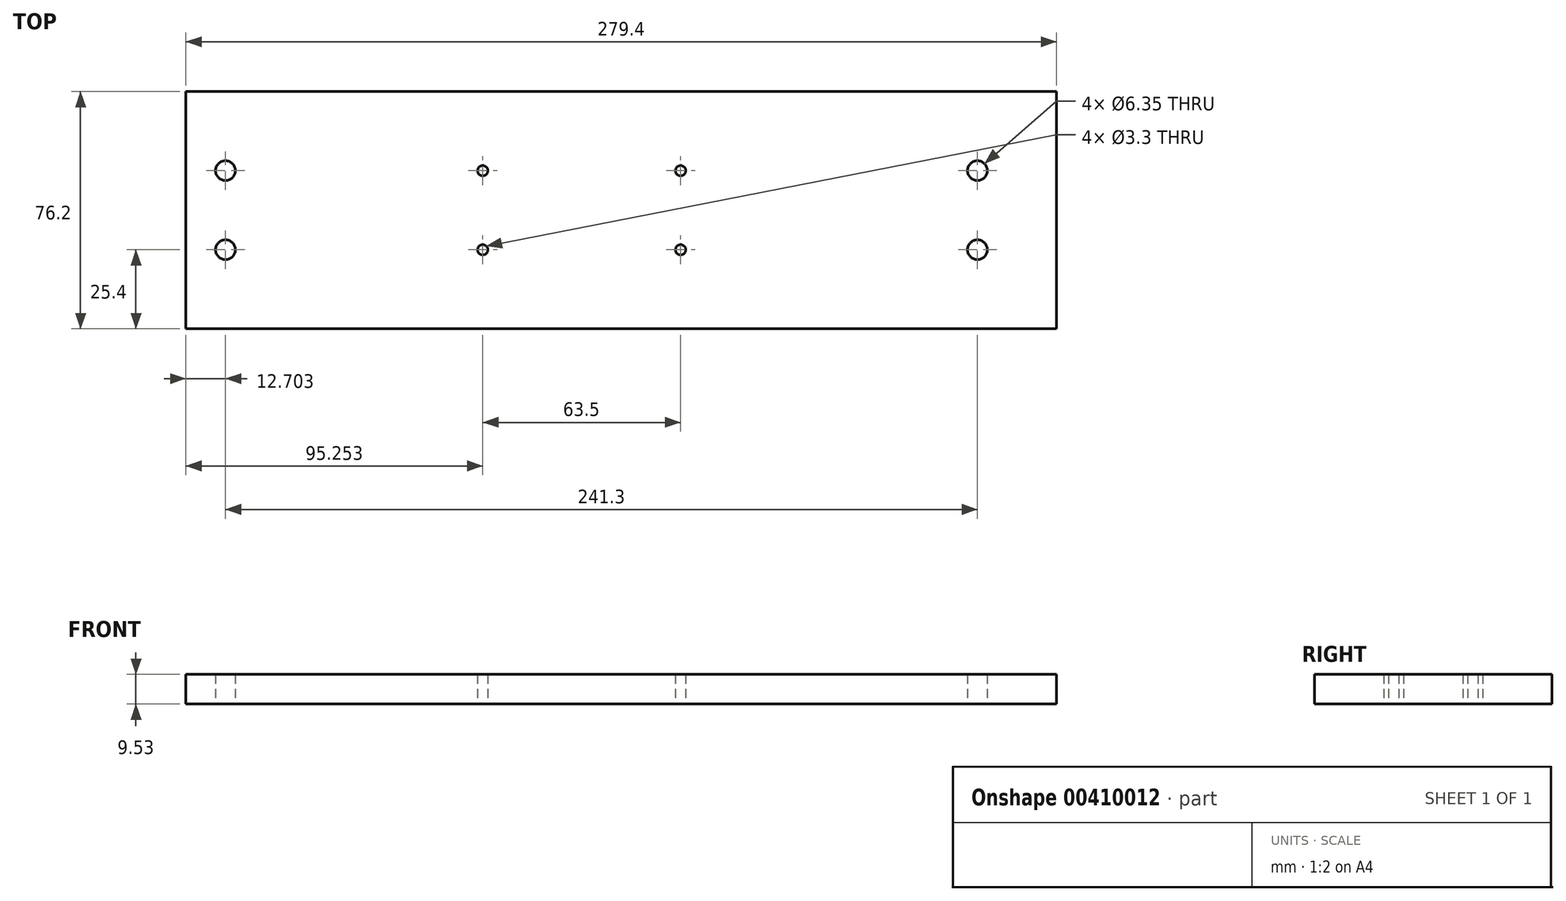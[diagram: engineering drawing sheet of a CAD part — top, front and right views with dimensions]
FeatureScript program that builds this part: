
annotation { "Feature Type Name" : "Feature", "Feature Type Description" : "" }
export const myFeature = defineFeature(function(context is Context, id is Id, definition is map)
    precondition{}
    {
        {
            var Q0;
            Q0=qCreatedBy(makeId("Top.planeOp"),FACE);
            var sketch = newSketch(context, id + "F0", { "sketchPlane" : qUnion([Q0])});
            skLineSegment(sketch, "E0.bottom", {"start": v(-134.22, 38.1) * mm, "end": v(145.18, 38.1) * mm});
            skLineSegment(sketch, "E0.top", {"start": v(-134.22, -38.1) * mm, "end": v(145.18, -38.1) * mm});
            skLineSegment(sketch, "E0.left", {"start": v(-134.22, 38.1) * mm, "end": v(-134.22, -38.1) * mm});
            skLineSegment(sketch, "E0.right", {"start": v(145.18, 38.1) * mm, "end": v(145.18, -38.1) * mm});
            skCircle(sketch, "E1", {"center": v(-121.52, 12.7) * mm, "radius": 3.18 * mm});
            skCircle(sketch, "E2", {"center": v(119.78, 12.7) * mm, "radius": 3.17 * mm});
            skCircle(sketch, "E3", {"center": v(-121.52, -12.7) * mm, "radius": 3.18 * mm});
            skCircle(sketch, "E4", {"center": v(119.78, -12.7) * mm, "radius": 3.18 * mm});
            skCircle(sketch, "E5", {"center": v(-38.97, 12.7) * mm, "radius": 1.65 * mm});
            skCircle(sketch, "E6", {"center": v(24.53, 12.7) * mm, "radius": 1.65 * mm});
            skCircle(sketch, "E7", {"center": v(-38.97, -12.7) * mm, "radius": 1.65 * mm});
            skCircle(sketch, "E8", {"center": v(24.53, -12.7) * mm, "radius": 1.65 * mm});
            skSolve(sketch);
        }
        {
            var Q0;
            Q0 = qSketchRegion(id + "F0", true);
            extrude(context, id + "F1", {"entities" : qUnion([Q0]), "depth" : 9.52 * mm});
        }
    });
